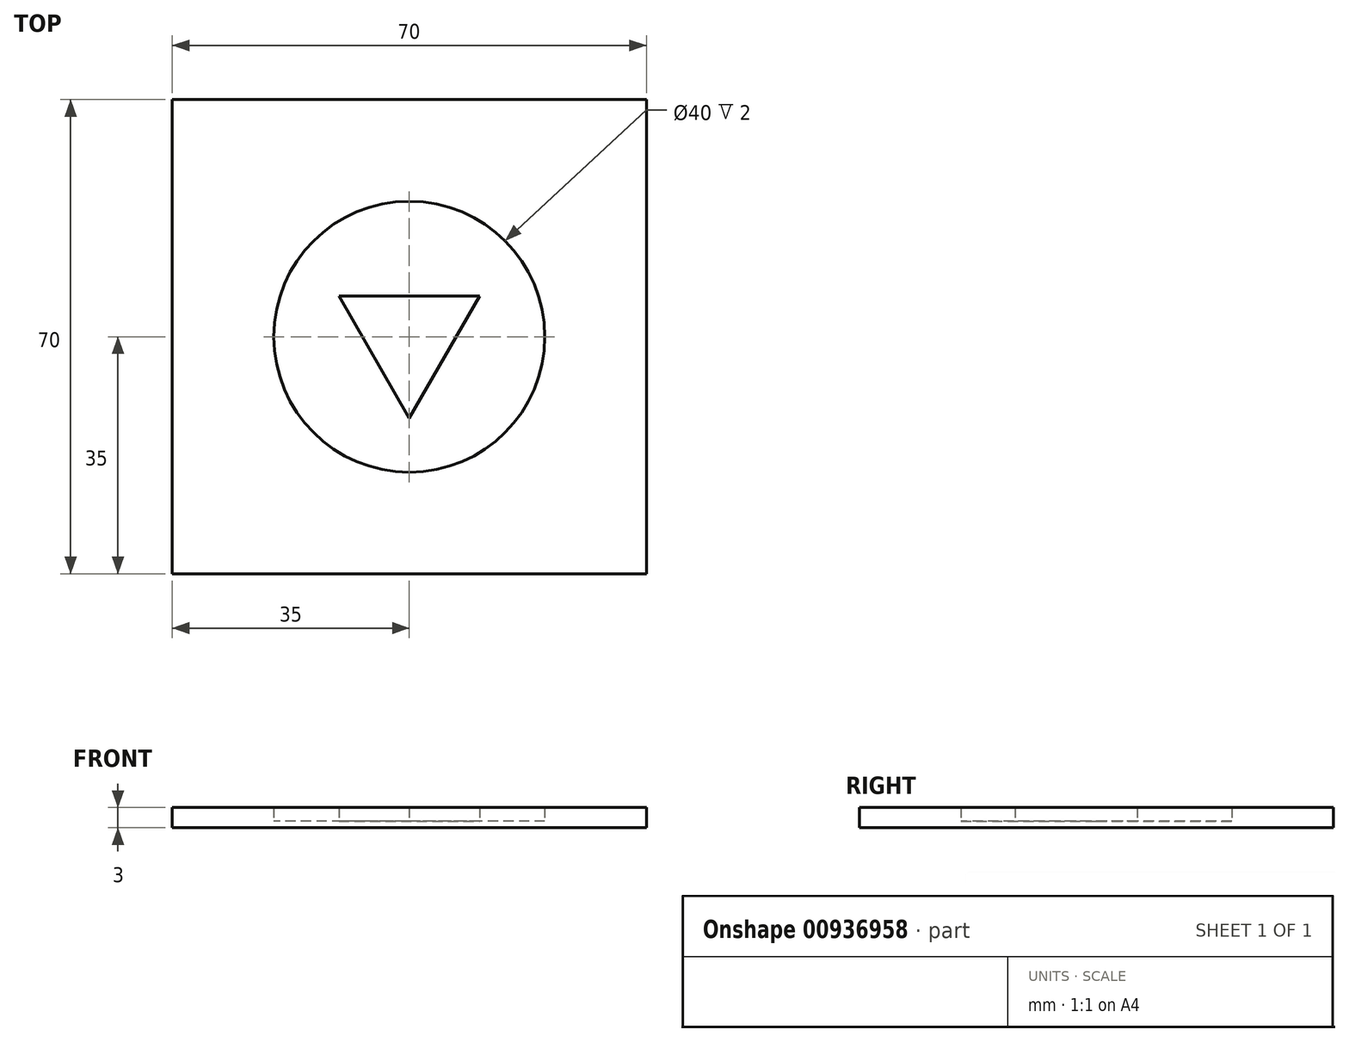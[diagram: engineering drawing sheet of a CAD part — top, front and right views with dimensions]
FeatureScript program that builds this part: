
annotation { "Feature Type Name" : "Feature", "Feature Type Description" : "" }
export const myFeature = defineFeature(function(context is Context, id is Id, definition is map)
    precondition{}
    {
        {
            var Q0;
            Q0=qCreatedBy(makeId("Top.planeOp"),FACE);
            var sketch = newSketch(context, id + "F0", { "sketchPlane" : qUnion([Q0])});
            skCircle(sketch, "E0", {"center": v(0, 0) * mm, "radius": 20 * mm});
            skLineSegment(sketch, "E1.bottom", {"start": v(35, 35) * mm, "end": v(-35, 35) * mm});
            skLineSegment(sketch, "E1.top", {"start": v(35, -35) * mm, "end": v(-35, -35) * mm});
            skLineSegment(sketch, "E1.left", {"start": v(35, 35) * mm, "end": v(35, -35) * mm});
            skLineSegment(sketch, "E1.right", {"start": v(-35, 35) * mm, "end": v(-35, -35) * mm});
            skLineSegment(sketch, "E2.0", {"start": v(-10.4, 6) * mm, "end": v(10.4, 6) * mm});
            skLineSegment(sketch, "E2.1", {"start": v(10.4, 6) * mm, "end": v(0, -12) * mm});
            skLineSegment(sketch, "E2.2", {"start": v(0, -12) * mm, "end": v(-10.4, 6) * mm});
            skPoint(sketch, "E2.0.midPoint", {"position": v(0, 6) * mm});
            skSolve(sketch);
        }
        {
            var Q0;
            Q0=makeQuery(id+"F0.imprint","IMPRINT",FACE,{"disambiguationData":[TD([[makeQuery(id+"F0.imprint","IMPRINT",EDGE,{"derivedFrom":sQuery(id+"F0.wireOp",EDGE,"d95cbc86-f329-403a-9f10-2cb31ffb93dc.0")}),1.0]])]});
            var Q1;
            Q1=makeQuery(id+"F0.imprint","IMPRINT",FACE,{"disambiguationData":[TD([[makeQuery(id+"F0.imprint","IMPRINT",EDGE,{"derivedFrom":sQuery(id+"F0.wireOp",EDGE,"E0")}),-1.0]])]});
            var Q2;
            Q2=makeQuery(id+"F0.imprint","IMPRINT",FACE,{"disambiguationData":[TD([[makeQuery(id+"F0.imprint","IMPRINT",EDGE,{"derivedFrom":sQuery(id+"F0.wireOp",EDGE,"E2.0")}),-1.0]])]});
            extrude(context, id + "F1", {"entities" : qUnion([Q0, Q1, Q2]), "depth" : 2 * mm, "offsetDistance" : 25 * mm});
        }
        {
            var Q0;
            Q0=makeQuery(id+"F0.imprint","IMPRINT",FACE,{"disambiguationData":[TD([[makeQuery(id+"F0.imprint","IMPRINT",EDGE,{"derivedFrom":sQuery(id+"F0.wireOp",EDGE,"E0")}),-1.0]])]});
            var Q1;
            Q1=makeQuery(id+"F0.imprint","IMPRINT",FACE,{"disambiguationData":[TD([[makeQuery(id+"F0.imprint","IMPRINT",EDGE,{"derivedFrom":sQuery(id+"F0.wireOp",EDGE,"E0")}),1.0]])]});
            var Q2;
            Q2=makeQuery(id+"F0.imprint","IMPRINT",FACE,{"disambiguationData":[TD([[makeQuery(id+"F0.imprint","IMPRINT",EDGE,{"derivedFrom":sQuery(id+"F0.wireOp",EDGE,"d95cbc86-f329-403a-9f10-2cb31ffb93dc.0")}),1.0]])]});
            var Q3;
            Q3=makeQuery(id+"F0.imprint","IMPRINT",FACE,{"disambiguationData":[TD([[makeQuery(id+"F0.imprint","IMPRINT",EDGE,{"derivedFrom":sQuery(id+"F0.wireOp",EDGE,"E2.0")}),-1.0]])]});
            extrude(context, id + "F2", {"entities" : qUnion([Q0, Q1, Q2, Q3]), "operationType" : NewBodyOperationType.ADD, "oppositeDirection" : true, "depth" : 1 * mm, "offsetDistance" : 25 * mm});
        }
    });
